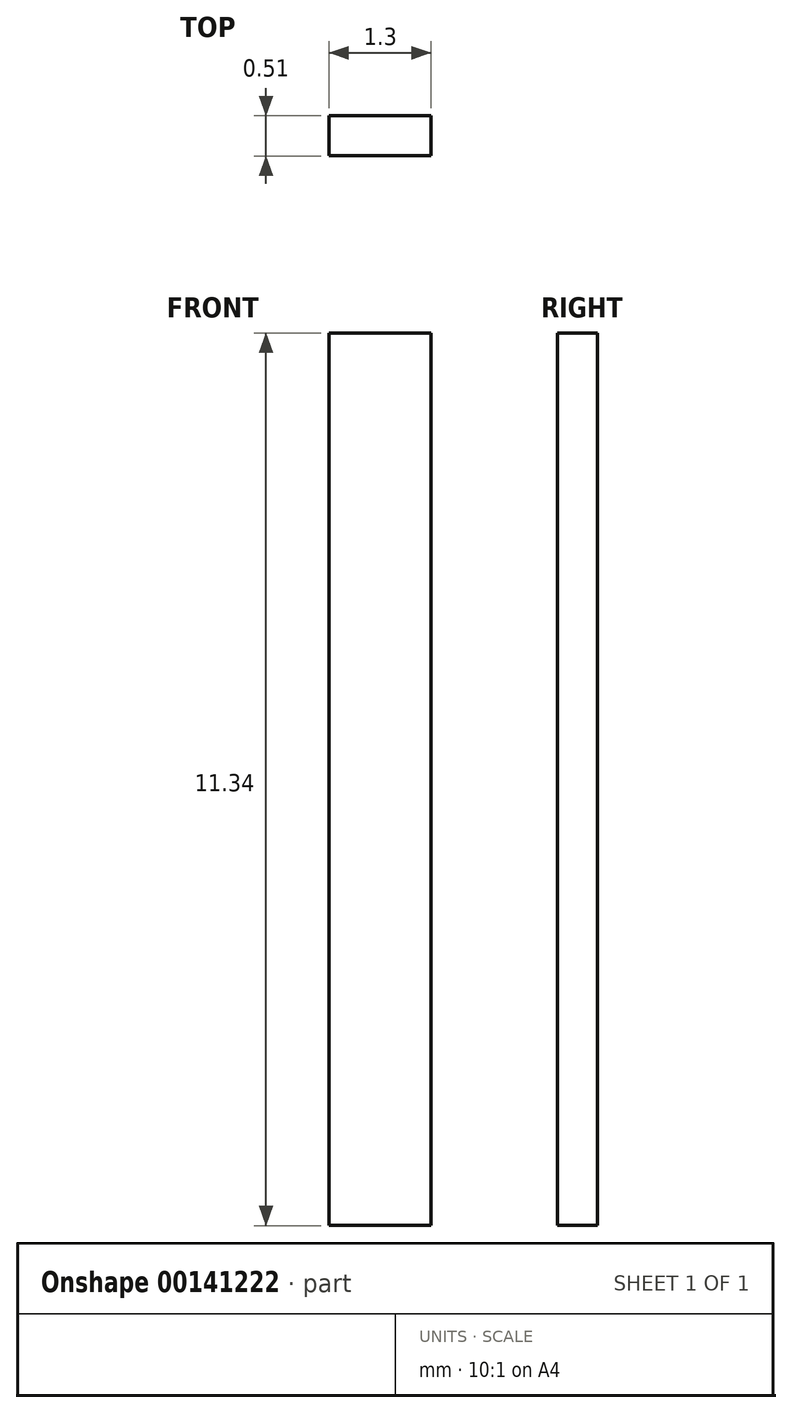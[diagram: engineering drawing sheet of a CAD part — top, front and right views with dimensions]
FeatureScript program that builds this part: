
annotation { "Feature Type Name" : "Feature", "Feature Type Description" : "" }
export const myFeature = defineFeature(function(context is Context, id is Id, definition is map)
    precondition{}
    {
        {
            var Q0;
            Q0=qCreatedBy(makeId("Front.planeOp"),FACE);
            var sketch = newSketch(context, id + "F0", { "sketchPlane" : qUnion([Q0])});
            skLineSegment(sketch, "E0.bottom", {"start": v(-46, 43.73) * mm, "end": v(-44.7, 43.73) * mm});
            skLineSegment(sketch, "E0.top", {"start": v(-46, 32.4) * mm, "end": v(-44.7, 32.4) * mm});
            skLineSegment(sketch, "E0.left", {"start": v(-46, 43.73) * mm, "end": v(-46, 32.4) * mm});
            skLineSegment(sketch, "E0.right", {"start": v(-44.7, 43.73) * mm, "end": v(-44.7, 32.4) * mm});
            skSolve(sketch);
        }
        {
            var Q0;
            Q0 = qSketchRegion(id + "F0", true);
            extrude(context, id + "F1", {"entities" : qUnion([Q0]), "depth" : 0.5 * mm});
        }
    });
